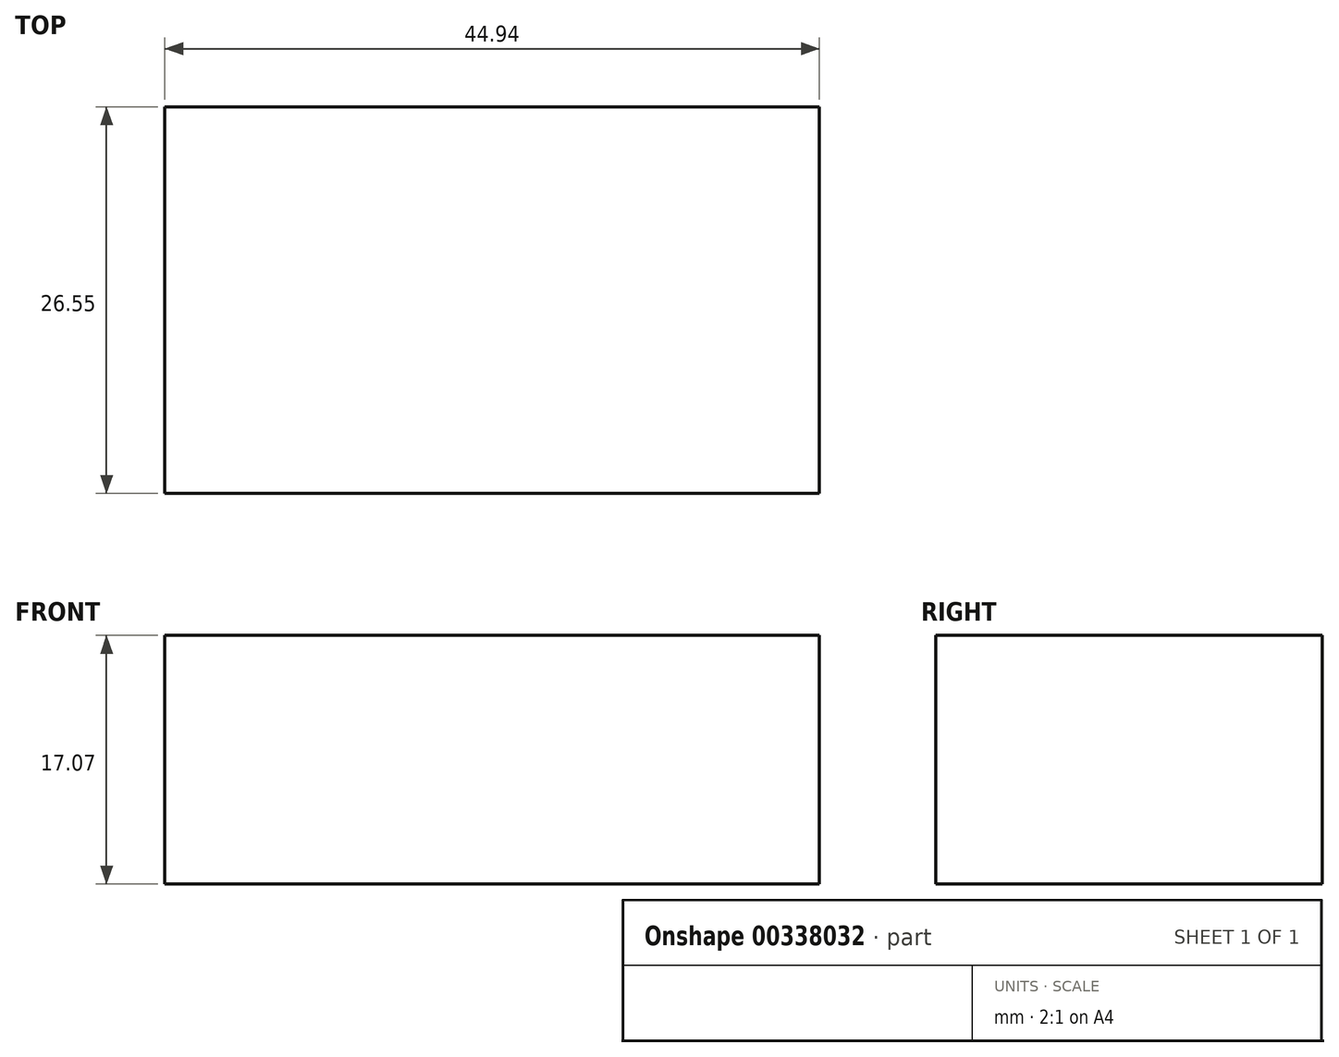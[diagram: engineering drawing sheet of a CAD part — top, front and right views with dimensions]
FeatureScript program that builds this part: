
annotation { "Feature Type Name" : "Feature", "Feature Type Description" : "" }
export const myFeature = defineFeature(function(context is Context, id is Id, definition is map)
    precondition{}
    {
        {
            var Q0;
            Q0=qCreatedBy(makeId("Top.planeOp"),FACE);
            var sketch = newSketch(context, id + "F0", { "sketchPlane" : qUnion([Q0])});
            skLineSegment(sketch, "E0.bottom", {"start": v(-22.48, 117.95) * mm, "end": v(22.47, 117.95) * mm});
            skLineSegment(sketch, "E0.top", {"start": v(-22.48, 144.5) * mm, "end": v(22.47, 144.5) * mm});
            skLineSegment(sketch, "E0.left", {"start": v(-22.48, 117.95) * mm, "end": v(-22.48, 144.5) * mm});
            skLineSegment(sketch, "E0.right", {"start": v(22.47, 117.95) * mm, "end": v(22.47, 144.5) * mm});
            skPoint(sketch, "E0.middle", {"position": v(0, 131.22) * mm});
            skSolve(sketch);
        }
        {
            var Q0;
            Q0=qSketchRegion(id+"F0",true);
            extrude(context, id + "F1", {"entities" : qUnion([Q0]), "depth" : 17.07 * mm});
        }
    });
